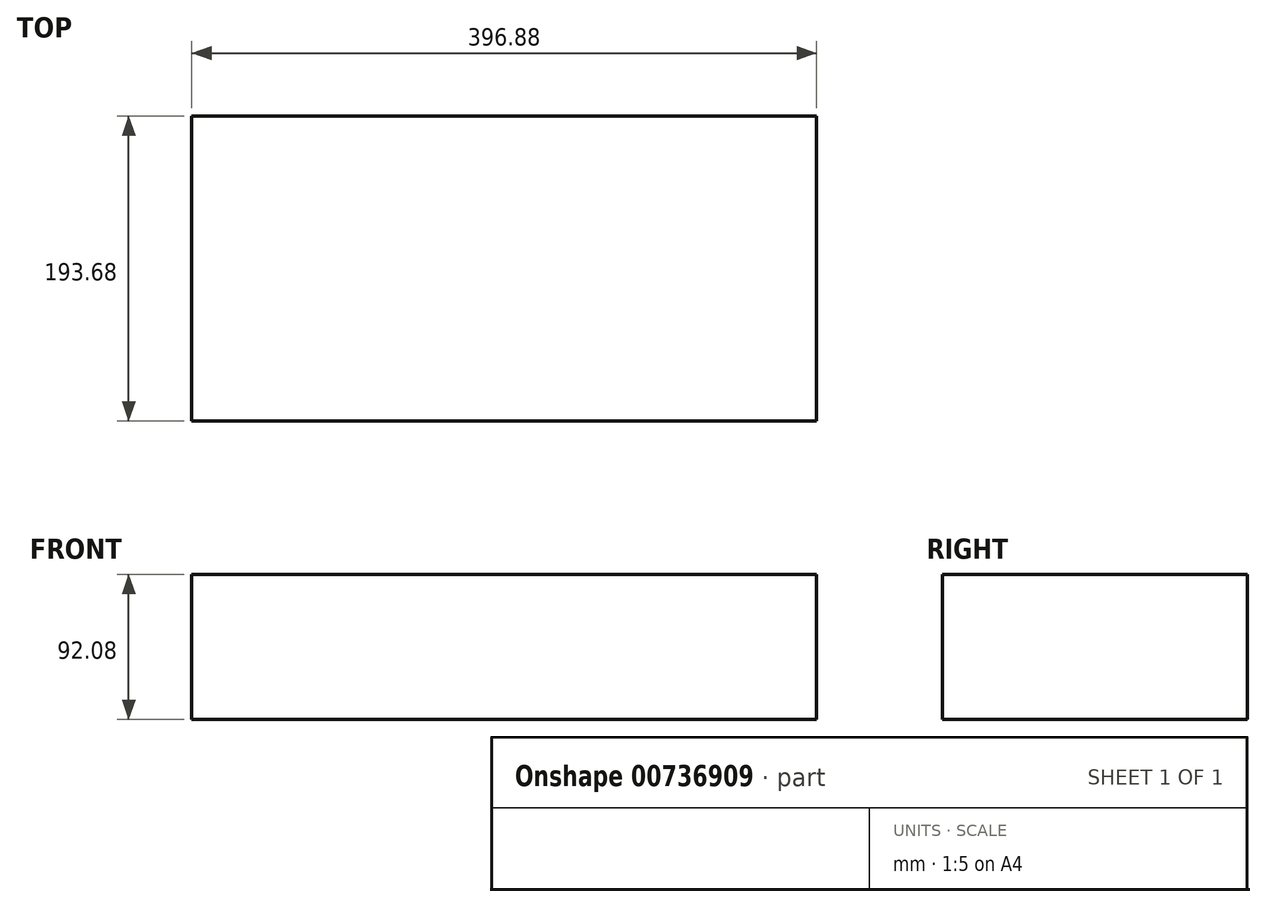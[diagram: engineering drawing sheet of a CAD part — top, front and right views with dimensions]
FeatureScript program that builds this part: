
annotation { "Feature Type Name" : "Feature", "Feature Type Description" : "" }
export const myFeature = defineFeature(function(context is Context, id is Id, definition is map)
    precondition{}
    {
        {
            var Q0;
            Q0=qCreatedBy(makeId("Top.planeOp"),FACE);
            var sketch = newSketch(context, id + "F0", { "sketchPlane" : qUnion([Q0])});
            skLineSegment(sketch, "E0.bottom", {"start": v(0, 0) * mm, "end": v(396.88, 0) * mm});
            skLineSegment(sketch, "E0.top", {"start": v(0, 193.68) * mm, "end": v(396.88, 193.68) * mm});
            skLineSegment(sketch, "E0.left", {"start": v(0, 0) * mm, "end": v(0, 193.68) * mm});
            skLineSegment(sketch, "E0.right", {"start": v(396.88, 0) * mm, "end": v(396.88, 193.68) * mm});
            skSolve(sketch);
        }
        {
            var Q0;
            Q0=makeQuery(id+"F0.imprint","IMPRINT",FACE,{"disambiguationData":[TD([[makeQuery(id+"F0.imprint","IMPRINT",EDGE,{"derivedFrom":sQuery(id+"F0.wireOp",EDGE,"E0.bottom")}),1.0]])]});
            extrude(context, id + "F1", {"entities" : qUnion([Q0]), "depth" : 92.07 * mm, "offsetDistance" : 25.4 * mm});
        }
    });
